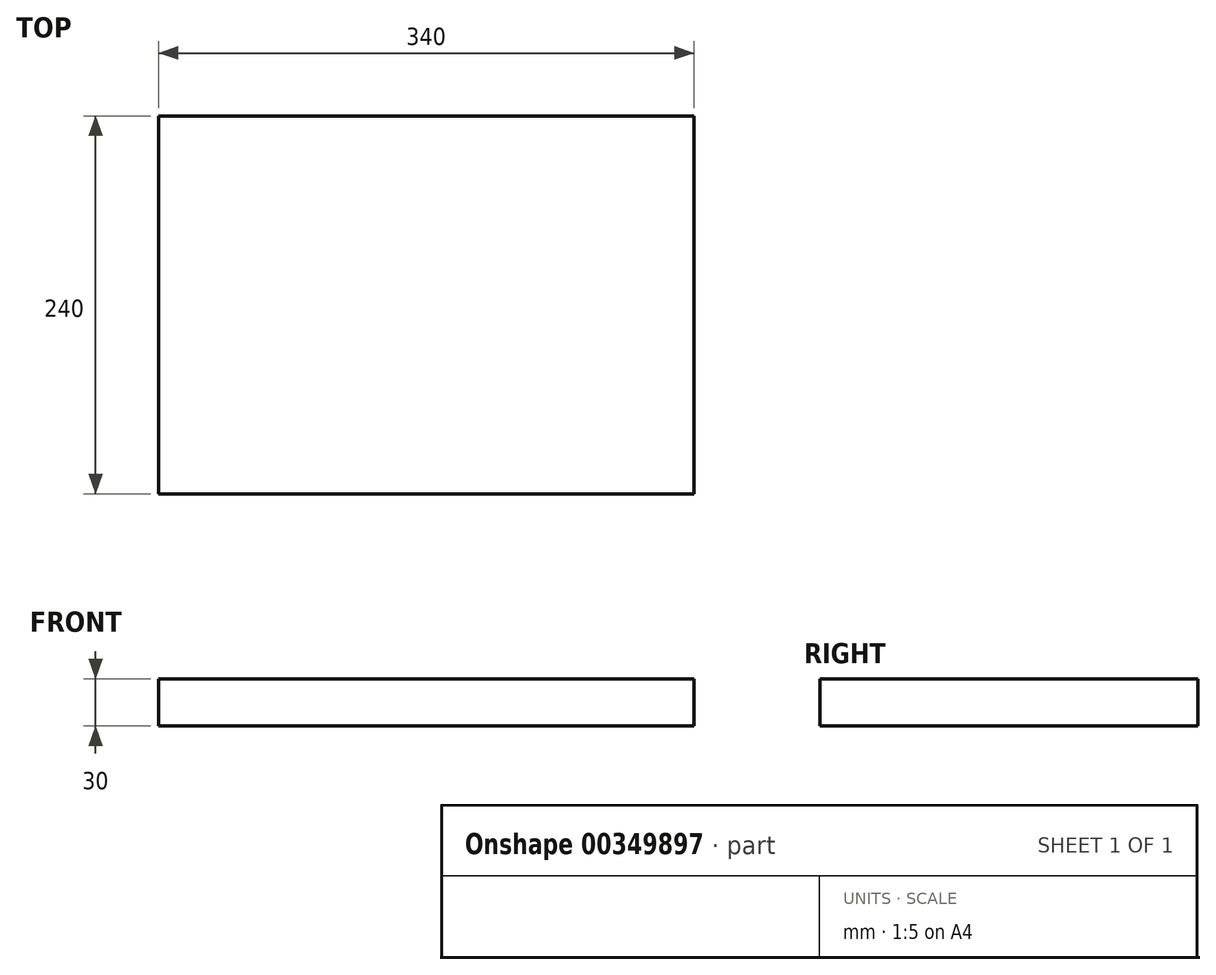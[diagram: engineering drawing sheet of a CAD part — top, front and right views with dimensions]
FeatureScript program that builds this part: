
annotation { "Feature Type Name" : "Feature", "Feature Type Description" : "" }
export const myFeature = defineFeature(function(context is Context, id is Id, definition is map)
    precondition{}
    {
        {
            var Q0;
            Q0=qCreatedBy(makeId("Top.planeOp"),FACE);
            var sketch = newSketch(context, id + "F0", { "sketchPlane" : qUnion([Q0])});
            skLineSegment(sketch, "E0.bottom", {"start": v(170, -120) * mm, "end": v(-170, -120) * mm});
            skLineSegment(sketch, "E0.top", {"start": v(170, 120) * mm, "end": v(-170, 120) * mm});
            skLineSegment(sketch, "E0.left", {"start": v(170, -120) * mm, "end": v(170, 120) * mm});
            skLineSegment(sketch, "E0.right", {"start": v(-170, -120) * mm, "end": v(-170, 120) * mm});
            skPoint(sketch, "E0.middle", {"position": v(0, 0) * mm});
            skSolve(sketch);
        }
        {
            var Q0;
            Q0 = qSketchRegion(id + "F0", true);
            extrude(context, id + "F1", {"entities" : qUnion([Q0]), "depth" : 30 * mm});
        }
    });
